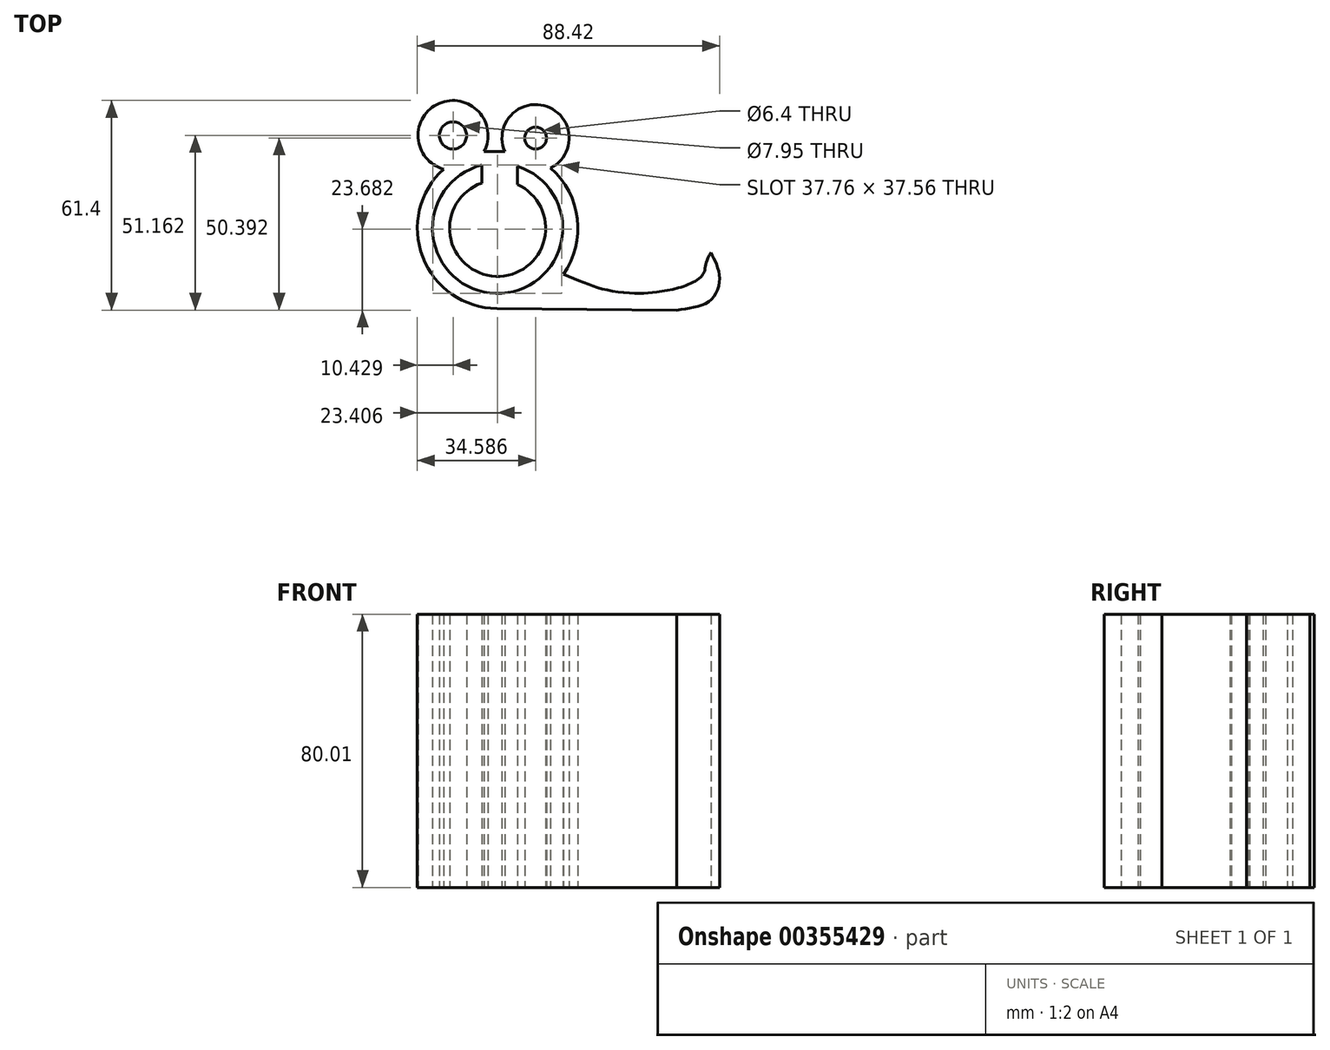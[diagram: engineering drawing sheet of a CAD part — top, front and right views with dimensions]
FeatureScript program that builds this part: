
annotation { "Feature Type Name" : "Feature", "Feature Type Description" : "" }
export const myFeature = defineFeature(function(context is Context, id is Id, definition is map)
    precondition{}
    {
        {
            var Q0;
            Q0=qCreatedBy(makeId("Top.planeOp"),FACE);
            var sketch = newSketch(context, id + "F0", { "sketchPlane" : qUnion([Q0])});
            skCircle(sketch, "E0", {"center": v(-62.17, 40.7) * mm, "radius": 10.23 * mm});
            skCircle(sketch, "E1", {"center": v(-38.01, 39.92) * mm, "radius": 9.83 * mm});
            skCircle(sketch, "E2", {"center": v(-62.17, 40.7) * mm, "radius": 3.98 * mm});
            skCircle(sketch, "E3", {"center": v(-38.01, 39.92) * mm, "radius": 3.2 * mm});
            skLineSegment(sketch, "E4", {"start": v(-52.02, 39.4) * mm, "end": v(-58.4, 39.4) * mm});
            skLineSegment(sketch, "E5", {"start": v(-47.84, 39.92) * mm, "end": v(-41.21, 39.92) * mm});
            skLineSegment(sketch, "E6", {"start": v(-53.1, 35.95) * mm, "end": v(-47, 35.95) * mm});
            skArc(sketch, "E7", {"start": v(-64.95, 30.84) * mm, "mid": v(-48.9, -9.99) * mm, "end": v(-33.61, 31.14) * mm});
            skLineSegment(sketch, "E8", {"start": v(-49.34, -9.99) * mm, "end": v(3.26, -10.47) * mm});
            skPoint(sketch, "E8.startSnap0", {"position": v(-48.9, -9.99) * mm});
            skFitSpline(sketch, "E9", {"points": [v(3.26, -10.47) * mm, v(13.07, -7.63) * mm, v(15.75, 0) * mm, v(13.37, 6.36) * mm, v(10.97, 10.52) * mm], "startDerivative": vector(35.77, 6.65) * mm, "endDerivative": vector(-23.42, 17.37) * mm});
            skFitSpline(sketch, "E10", {"points": [v(13.37, 6.36) * mm, v(10.97, 0) * mm, v(3.82, -3.92) * mm, v(-3.6, -5.25) * mm, v(-8.65, -5.54) * mm, v(-16.68, -4.65) * mm, v(-22.64, -2.87) * mm, v(-29.9, 0) * mm], "startDerivative": vector(-46.16, -63.47) * mm, "endDerivative": vector(-50.6, 20.24) * mm});
            skLineSegment(sketch, "E11", {"start": v(3.82, -3.92) * mm, "end": v(6.77, -9.82) * mm});
            skCircle(sketch, "E12", {"center": v(-49.12, 13.5) * mm, "radius": 19.07 * mm});
            skLineSegment(sketch, "E13", {"start": v(-53.79, 31.99) * mm, "end": v(-53.79, 26.76) * mm});
            skLineSegment(sketch, "E14", {"start": v(-43.38, 31.69) * mm, "end": v(-43.38, 26.34) * mm});
            skCircle(sketch, "E15", {"center": v(-49.12, 13.5) * mm, "radius": 14.06 * mm});
            skSolve(sketch);
        }
        {
            var Q0;
            Q0 = qSketchRegion(id + "F0", true);
            var Q1;
            {var subQ0=sQuery(id+"F0.wireOp",EDGE,"E15");var subQ1=makeQuery(id+"F0.imprint","INTERSECT",VERTEX,{"derivedFrom":[sQuery(id+"F0.wireOp",EDGE,"E13"),subQ0]});Q1=makeQuery(id+"F0.imprint","IMPRINT",FACE,{"disambiguationData":[TD([[makeQuery(id+"F0.imprint","IMPRINT",EDGE,{"disambiguationData":[TD([[subQ1,1.0]])],"derivedFrom":subQ0}),1.0]])]});}
            var Q2;
            {var subQ0=sQuery(id+"F0.wireOp",EDGE,"E13");Q2=makeQuery(id+"F0.imprint","IMPRINT",FACE,{"disambiguationData":[TD([[makeQuery(id+"F0.imprint","IMPRINT",EDGE,{"derivedFrom":subQ0}),1.0]])]});}
            extrude(context, id + "F1", {"entities" : qUnion([Q0, Q1, Q2]), "depth" : 80 * mm});
        }
    });
